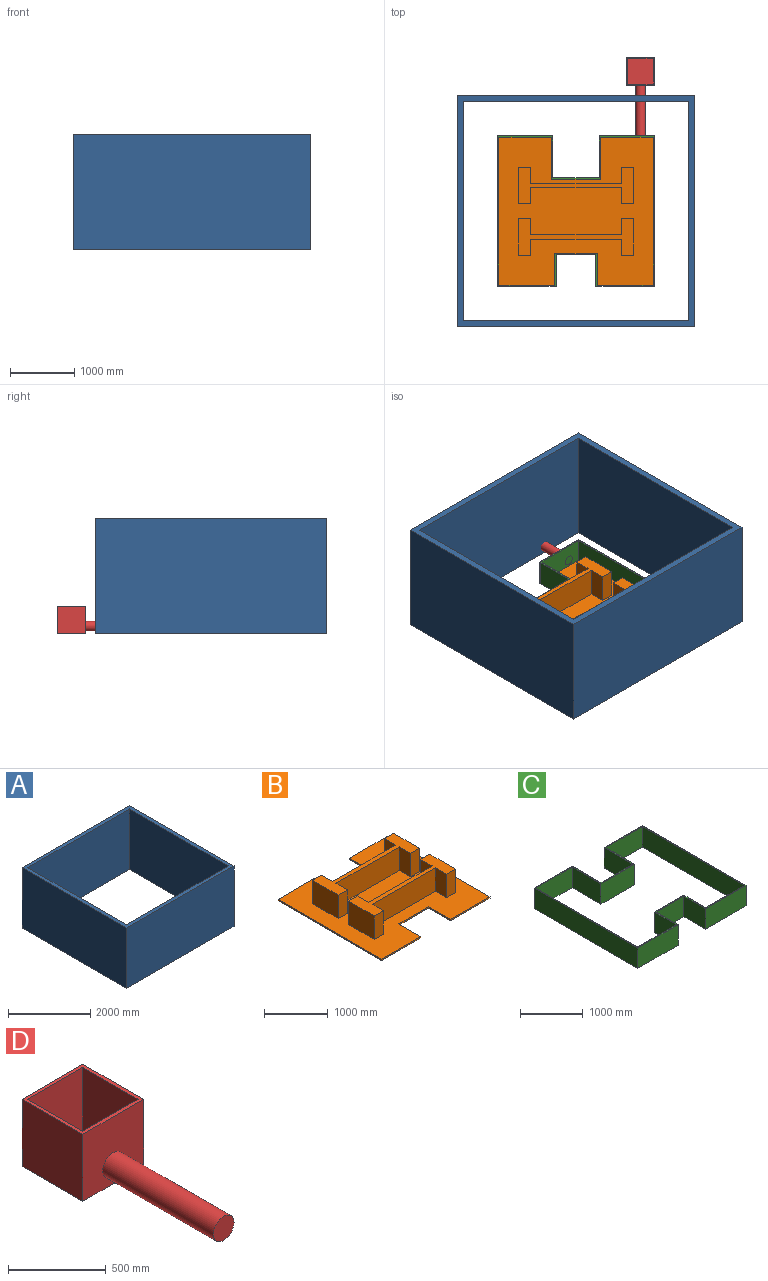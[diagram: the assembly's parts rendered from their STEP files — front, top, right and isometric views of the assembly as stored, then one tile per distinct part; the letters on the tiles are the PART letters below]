
ASSEMBLY  parts=4 mates=3
PART A: 10 faces, bbox 3700x3600x1800 mm
  f0: plane 3600x1800mm, normal (-1,0,0), area 6480000mm2, adj f1,f7,f8,f9
  f1: plane 3700x1800mm, normal (0,-1,0), area 6660000mm2, adj f0,f2,f8,f9
  f2: plane 3600x1800mm, normal (1,0,0), area 6480000mm2, adj f1,f7,f8,f9
  f3: plane 3400x1800mm, normal (-1,0,0), area 6120000mm2, adj f4,f6,f8,f9
  f4: plane 3500x1800mm, normal (0,1,0), area 6300000mm2, adj f3,f5,f8,f9
  f5: plane 3400x1800mm, normal (1,0,0), area 6120000mm2, adj f4,f6,f8,f9
  f6: plane 3500x1800mm, normal (0,-1,0), area 6300000mm2, adj f3,f5,f8,f9
  f7: plane 3700x1800mm, normal (0,1,0), area 6660000mm2, adj f0,f2,f8,f9
  f8: plane 3700x3600mm, normal (0,0,1), area 1420000mm2, adj f0,f1,f2,f3,f4,f5,f6,f7
  f9: plane 3700x3600mm, normal (0,0,-1), area 1420000mm2, adj f0,f1,f2,f3,f4,f5,f6,f7
PART B: 40 faces, bbox 2400x2300x475 mm
  f0: plane 1400x450mm, normal (0,1,0), area 630000mm2, adj f1,f20,f34,f39
  f1: plane 2400x2300mm, normal (0,0,1), area 4050600mm2, adj f0,f2,f3,f4,f5,f6,f7,f8
  f2: plane 1400x450mm, normal (0,-1,0), area 630000mm2, adj f1,f20,f32,f36
  f3: plane 1400x450mm, normal (0,1,0), area 630000mm2, adj f1,f23,f24,f31
  f4: plane 1400x450mm, normal (0,-1,0), area 630000mm2, adj f1,f23,f26,f28
  f5: plane 820x25mm, normal (0,1,0), area 20500mm2, adj f1,f6,f16,f17
  f6: plane 2300x25mm, normal (1,0,0), area 57500mm2, adj f1,f5,f7,f17
  f7: plane 870x25mm, normal (0,-1,0), area 21750mm2, adj f1,f6,f8,f17
  f8: plane 490x25mm, normal (-1,0,0), area 12250mm2, adj f1,f7,f9,f17
  f9: plane 660x25mm, normal (0,-1,0), area 16500mm2, adj f1,f8,f10,f17
  f10: plane 490x25mm, normal (1,0,0), area 12250mm2, adj f1,f9,f11,f17
  f11: plane 870x25mm, normal (0,-1,0), area 21750mm2, adj f1,f10,f12,f17
  f12: plane 2300x25mm, normal (-1,0,0), area 57500mm2, adj f1,f11,f13,f17
  f13: plane 820x25mm, normal (0,1,0), area 20500mm2, adj f1,f12,f14,f17
  f14: plane 650x25mm, normal (1,0,0), area 16250mm2, adj f1,f13,f15,f17
  f15: plane 760x25mm, normal (0,1,0), area 19000mm2, adj f1,f14,f16,f17
  f16: plane 650x25mm, normal (-1,0,0), area 16250mm2, adj f1,f5,f15,f17
  f17: plane 2400x2300mm, normal (0,0,-1), area 4702600mm2, adj f5,f6,f7,f8,f9,f10,f11,f12
  f18: plane 570x450mm, normal (-1,0,0), area 256500mm2, adj f1,f20,f33,f35
  f19: plane 570x450mm, normal (1,0,0), area 256500mm2, adj f1,f20,f37,f38
  f20: plane 1800x570mm, normal (0,0,1), area 326000mm2, adj f0,f2,f18,f19,f32,f33,f34,f35
  f21: plane 570x450mm, normal (1,0,0), area 256500mm2, adj f1,f23,f29,f30
  f22: plane 570x450mm, normal (-1,0,0), area 256500mm2, adj f1,f23,f25,f27
  f23: plane 1800x570mm, normal (0,0,1), area 326000mm2, adj f3,f4,f21,f22,f24,f25,f26,f27
  f24: plane 450x250mm, normal (1,0,0), area 112500mm2, adj f1,f3,f23,f25
  f25: plane 450x200mm, normal (0,1,0), area 90000mm2, adj f1,f22,f23,f24
  f26: plane 450x250mm, normal (1,0,0), area 112500mm2, adj f1,f4,f23,f27
  f27: plane 450x200mm, normal (0,-1,0), area 90000mm2, adj f1,f22,f23,f26
  f28: plane 450x250mm, normal (-1,0,0), area 112500mm2, adj f1,f4,f23,f29
  f29: plane 450x200mm, normal (0,-1,0), area 90000mm2, adj f1,f21,f23,f28
  f30: plane 450x200mm, normal (0,1,0), area 90000mm2, adj f1,f21,f23,f31
  f31: plane 450x250mm, normal (-1,0,0), area 112500mm2, adj f1,f3,f23,f30
  f32: plane 450x250mm, normal (1,0,0), area 112500mm2, adj f1,f2,f20,f33
  f33: plane 450x200mm, normal (0,-1,0), area 90000mm2, adj f1,f18,f20,f32
  f34: plane 450x250mm, normal (1,0,0), area 112500mm2, adj f0,f1,f20,f35
  f35: plane 450x200mm, normal (0,1,0), area 90000mm2, adj f1,f18,f20,f34
  f36: plane 450x250mm, normal (-1,0,0), area 112500mm2, adj f1,f2,f20,f37
  f37: plane 450x200mm, normal (0,-1,0), area 90000mm2, adj f1,f19,f20,f36
  f38: plane 450x200mm, normal (0,1,0), area 90000mm2, adj f1,f19,f20,f39
  f39: plane 450x250mm, normal (-1,0,0), area 112500mm2, adj f0,f1,f20,f38
PART C: 26 faces, bbox 2440x2340x400 mm
  f0: plane 2340x400mm, normal (1,0,0), area 936000mm2, adj f1,f23,f24,f25
  f1: plane 860x400mm, normal (0,1,0), area 344000mm2, adj f0,f2,f24,f25
  f2: plane 650x400mm, normal (-1,0,0), area 260000mm2, adj f1,f3,f24,f25
  f3: plane 720x400mm, normal (0,1,0), area 288000mm2, adj f2,f4,f24,f25
  f4: plane 650x400mm, normal (1,0,0), area 260000mm2, adj f3,f5,f24,f25
  f5: plane 860x400mm, normal (0,1,0), area 344000mm2, adj f4,f6,f24,f25
  f6: plane 2340x400mm, normal (-1,0,0), area 936000mm2, adj f5,f7,f24,f25
  f7: plane 910x400mm, normal (0,-1,0), area 364000mm2, adj f6,f8,f24,f25
  f8: plane 490x400mm, normal (1,0,0), area 196000mm2, adj f7,f9,f24,f25
  f9: plane 620x400mm, normal (0,-1,0), area 248000mm2, adj f8,f10,f24,f25
  f10: plane 490x400mm, normal (-1,0,0), area 196000mm2, adj f9,f23,f24,f25
  f11: plane 820x400mm, normal (0,-1,0), area 328000mm2, adj f12,f22,f24,f25
  f12: plane 2300x400mm, normal (-1,0,0), area 920000mm2, adj f11,f13,f24,f25
  f13: plane 870x400mm, normal (0,1,0), area 348000mm2, adj f12,f14,f24,f25
  f14: plane 490x400mm, normal (1,0,0), area 196000mm2, adj f13,f15,f24,f25
  f15: plane 660x400mm, normal (0,1,0), area 264000mm2, adj f14,f16,f24,f25
  f16: plane 490x400mm, normal (-1,0,0), area 196000mm2, adj f15,f17,f24,f25
  f17: plane 870x400mm, normal (0,1,0), area 348000mm2, adj f16,f18,f24,f25
  f18: plane 2300x400mm, normal (1,0,0), area 920000mm2, adj f17,f19,f24,f25
  f19: plane 820x400mm, normal (0,-1,0), area 328000mm2, adj f18,f20,f24,f25
  f20: plane 650x400mm, normal (-1,0,0), area 260000mm2, adj f19,f21,f24,f25
  f21: plane 760x400mm, normal (0,-1,0), area 304000mm2, adj f20,f22,f24,f25
  f22: plane 650x400mm, normal (1,0,0), area 260000mm2, adj f11,f21,f24,f25
  f23: plane 910x400mm, normal (0,-1,0), area 364000mm2, adj f0,f10,f24,f25
  f24: plane 2440x2340mm, normal (0,0,1), area 235200mm2, adj f0,f1,f2,f3,f4,f5,f6,f7
  f25: plane 2440x2340mm, normal (0,0,-1), area 235200mm2, adj f0,f1,f2,f3,f4,f5,f6,f7
PART D: 13 faces, bbox 440x1240x420 mm
  f0: plane 440x420mm, normal (-1,0,0), area 184800mm2, adj f1,f7,f8,f12
  f1: plane 440x420mm, normal (0,-1,0), area 167128.5mm2, adj f0,f2,f8,f9,f12
  f2: plane 440x420mm, normal (1,0,0), area 184800mm2, adj f1,f7,f8,f12
  f3: plane 400x400mm, normal (-1,0,0), area 160000mm2, adj f4,f6,f8,f11
  f4: plane 400x400mm, normal (0,1,0), area 160000mm2, adj f3,f5,f8,f11
  f5: plane 400x400mm, normal (1,0,0), area 160000mm2, adj f4,f6,f8,f11
  f6: plane 400x400mm, normal (0,-1,0), area 160000mm2, adj f3,f5,f8,f11
  f7: plane 440x420mm, normal (0,1,0), area 184800mm2, adj f0,f2,f8,f12
  f8: plane 440x440mm, normal (0,0,1), area 33600mm2, adj f0,f1,f2,f3,f4,f5,f6,f7
  f9: cylinder r=75mm len=800mm, axis (0,1,0), area 376991.1mm2, adj f1,f10
  f10: plane 150x150mm, normal (0,-1,0), area 17671.5mm2, adj f9
  f11: plane 400x400mm, normal (0,0,1), area 160000mm2, adj f3,f4,f5,f6
  f12: plane 440x440mm, normal (0,0,-1), area 193600mm2, adj f0,f1,f2,f7
PLACE A t=(3.11,-0.29,-215.63)mm
PLACE B t=(3.11,-0.29,-215.63)mm fixed
PLACE C t=(3.11,-0.29,-215.63)mm fixed
PLACE D t=(1003.11,2176.28,-195.63)mm
MATE planar D.f12 <-> B.f17  axis (0,0,-1) through (1003.11,2176.28,-215.63)mm
MATE planar D.f2 <-> C.f0  axis (1,0,0) through (1223.11,2176.28,-5.63)mm
MATE planar A.f9 <-> B.f17  axis (0,0,-1) through (3.11,-0.29,-215.63)mm
